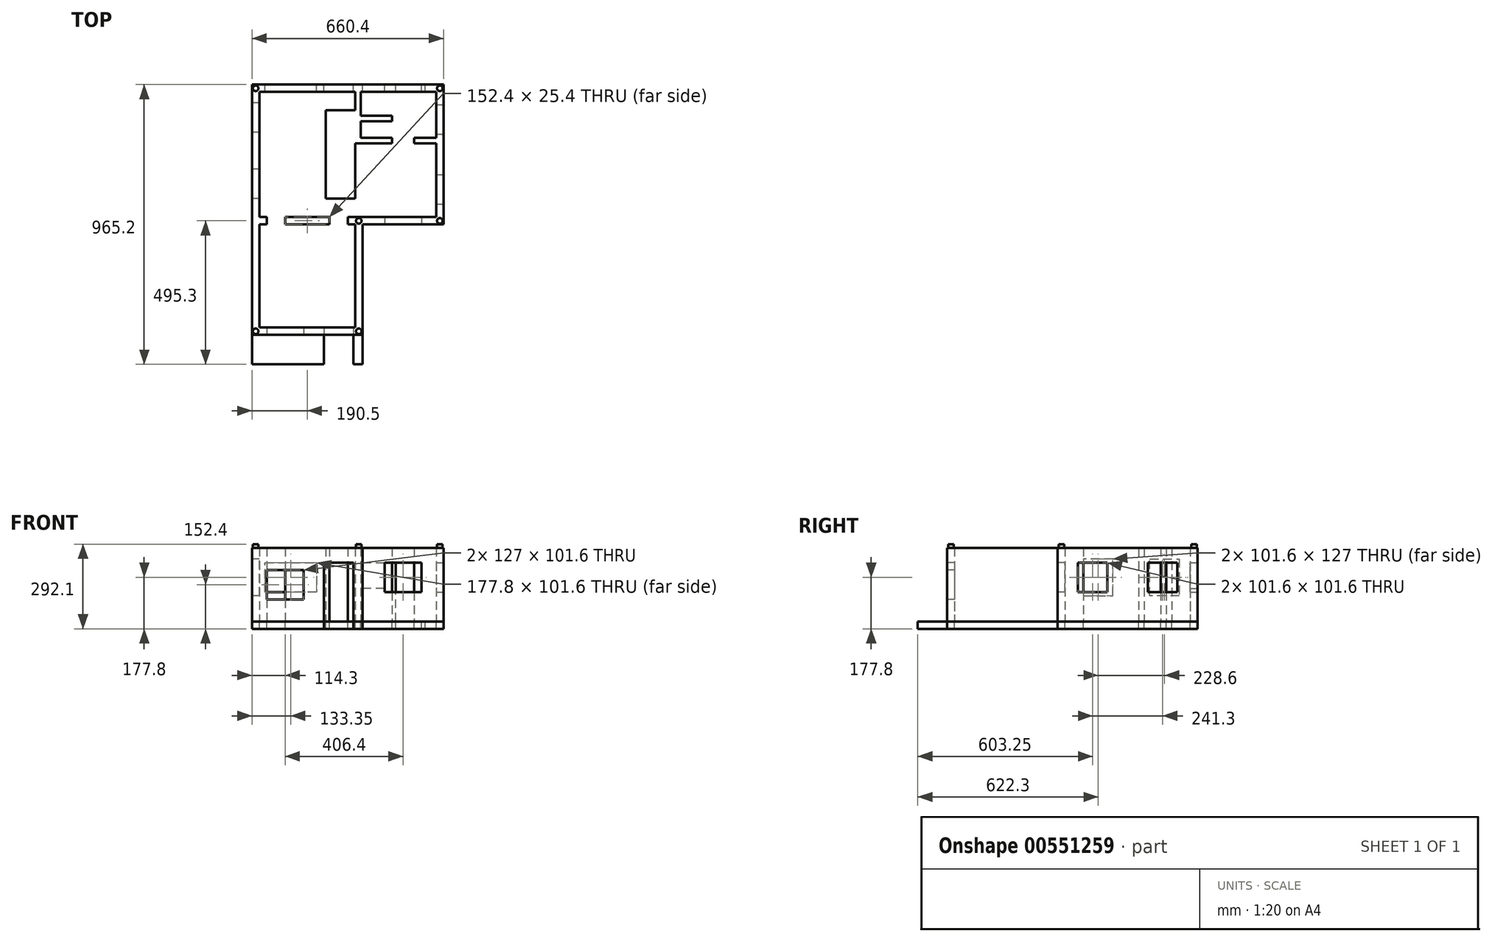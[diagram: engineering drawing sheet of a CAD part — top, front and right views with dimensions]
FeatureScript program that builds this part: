
annotation { "Feature Type Name" : "Feature", "Feature Type Description" : "" }
export const myFeature = defineFeature(function(context is Context, id is Id, definition is map)
    precondition{}
    {
        {
            var Q0;
            Q0=qCreatedBy(makeId("Top.planeOp"),FACE);
            var sketch = newSketch(context, id + "F0", { "sketchPlane" : qUnion([Q0])});
            skLineSegment(sketch, "E0", {"start": v(0, 0) * mm, "end": v(330.2, 0) * mm});
            skLineSegment(sketch, "E1", {"start": v(0, 0) * mm, "end": v(0, 381) * mm});
            skLineSegment(sketch, "E2", {"start": v(330.2, 0) * mm, "end": v(330.2, 381) * mm});
            skLineSegment(sketch, "E3", {"start": v(0, 381) * mm, "end": v(0, 812.8) * mm});
            skLineSegment(sketch, "E4", {"start": v(0, 812.8) * mm, "end": v(330.2, 812.8) * mm});
            skLineSegment(sketch, "E5", {"start": v(330.2, 381) * mm, "end": v(609.6, 381) * mm});
            skLineSegment(sketch, "E6", {"start": v(609.6, 381) * mm, "end": v(609.6, 812.8) * mm});
            skLineSegment(sketch, "E7", {"start": v(609.6, 635) * mm, "end": v(533.4, 635) * mm});
            skLineSegment(sketch, "E8", {"start": v(609.6, 812.8) * mm, "end": v(508, 812.8) * mm});
            skLineSegment(sketch, "E9", {"start": v(330.2, 812.8) * mm, "end": v(508, 812.8) * mm});
            skLineSegment(sketch, "E10", {"start": v(330.2, 672.42) * mm, "end": v(330.2, 812.8) * mm});
            skLineSegment(sketch, "E11", {"start": v(330.2, 635) * mm, "end": v(457.2, 635) * mm});
            skLineSegment(sketch, "E12", {"start": v(457.2, 711.2) * mm, "end": v(330.2, 711.2) * mm});
            skLineSegment(sketch, "E13", {"start": v(330.2, 0) * mm, "end": v(355.6, 0) * mm});
            skLineSegment(sketch, "E14", {"start": v(355.6, 0) * mm, "end": v(355.6, 355.6) * mm});
            skLineSegment(sketch, "E15", {"start": v(355.6, 355.6) * mm, "end": v(635, 355.6) * mm});
            skLineSegment(sketch, "E16", {"start": v(635, 355.6) * mm, "end": v(635, 838.2) * mm});
            skLineSegment(sketch, "E17", {"start": v(635, 838.2) * mm, "end": v(-25.4, 838.2) * mm});
            skLineSegment(sketch, "E18", {"start": v(-25.4, 838.2) * mm, "end": v(-25.4, -25.4) * mm});
            skLineSegment(sketch, "E19", {"start": v(-25.4, -25.4) * mm, "end": v(355.6, -25.4) * mm});
            skLineSegment(sketch, "E20", {"start": v(355.6, -25.4) * mm, "end": v(355.6, 0) * mm});
            skLineSegment(sketch, "E21", {"start": v(0, 381) * mm, "end": v(25.4, 381) * mm});
            skLineSegment(sketch, "E22", {"start": v(25.4, 381) * mm, "end": v(25.4, 355.6) * mm});
            skLineSegment(sketch, "E23", {"start": v(25.4, 355.6) * mm, "end": v(0, 355.6) * mm});
            skLineSegment(sketch, "E24", {"start": v(88.9, 381) * mm, "end": v(241.3, 381) * mm});
            skLineSegment(sketch, "E25", {"start": v(88.9, 381) * mm, "end": v(88.9, 355.6) * mm});
            skLineSegment(sketch, "E26", {"start": v(88.9, 355.6) * mm, "end": v(241.3, 355.6) * mm});
            skLineSegment(sketch, "E27", {"start": v(241.3, 355.6) * mm, "end": v(241.3, 381) * mm});
            skLineSegment(sketch, "E28", {"start": v(304.8, 355.6) * mm, "end": v(304.8, 381) * mm});
            skLineSegment(sketch, "E29", {"start": v(304.8, 381) * mm, "end": v(330.2, 381) * mm});
            skLineSegment(sketch, "E30", {"start": v(304.8, 355.6) * mm, "end": v(330.2, 355.6) * mm});
            skLineSegment(sketch, "E31", {"start": v(330.2, 672.42) * mm, "end": v(330.2, 635) * mm});
            skLineSegment(sketch, "E32", {"start": v(228.6, 749.3) * mm, "end": v(330.2, 749.3) * mm});
            skLineSegment(sketch, "E33", {"start": v(330.2, 635) * mm, "end": v(330.2, 444.5) * mm});
            skLineSegment(sketch, "E34", {"start": v(330.2, 444.5) * mm, "end": v(228.6, 444.5) * mm});
            skLineSegment(sketch, "E35", {"start": v(228.6, 444.5) * mm, "end": v(228.6, 749.3) * mm});
            skLineSegment(sketch, "E36", {"start": v(457.2, 711.2) * mm, "end": v(457.2, 730.25) * mm});
            skLineSegment(sketch, "E37", {"start": v(457.2, 635) * mm, "end": v(457.2, 654.05) * mm});
            skLineSegment(sketch, "E38", {"start": v(457.2, 654.05) * mm, "end": v(349.25, 654.05) * mm});
            skLineSegment(sketch, "E39", {"start": v(349.25, 654.05) * mm, "end": v(349.25, 711.2) * mm});
            skLineSegment(sketch, "E40", {"start": v(533.4, 635) * mm, "end": v(533.4, 654.05) * mm});
            skLineSegment(sketch, "E41", {"start": v(533.4, 654.05) * mm, "end": v(609.6, 654.05) * mm});
            skLineSegment(sketch, "E42", {"start": v(457.2, 730.25) * mm, "end": v(349.25, 730.25) * mm});
            skLineSegment(sketch, "E43", {"start": v(349.25, 730.25) * mm, "end": v(349.25, 812.8) * mm});
            skSolve(sketch);
        }
        {
            var Q0;
            {var subQ8=sQuery(id+"F0.wireOp",EDGE,"E0");Q0=makeQuery(id+"F0.imprint","IMPRINT",FACE,{"disambiguationData":[TD([[makeQuery(id+"F0.imprint","IMPRINT",EDGE,{"derivedFrom":subQ8}),-1.0]])]});}
            var Q1;
            Q1=makeQuery(id+"F0.imprint","IMPRINT",FACE,{"disambiguationData":[TD([[makeQuery(id+"F0.imprint","IMPRINT",EDGE,{"derivedFrom":sQuery(id+"F0.wireOp",EDGE,"E24")}),-1.0]])]});
            var Q2;
            {var subQ0=sQuery(id+"F0.wireOp",EDGE,"E21");Q2=makeQuery(id+"F0.imprint","IMPRINT",FACE,{"disambiguationData":[TD([[makeQuery(id+"F0.imprint","IMPRINT",EDGE,{"derivedFrom":subQ0}),-1.0]])]});}
            var Q3;
            Q3=makeQuery(id+"F0.imprint","IMPRINT",FACE,{"disambiguationData":[TD([[makeQuery(id+"F0.imprint","IMPRINT",EDGE,{"derivedFrom":sQuery(id+"F0.wireOp",EDGE,"E28")}),-1.0]])]});
            var Q4;
            {var subQ3=sQuery(id+"F0.wireOp",EDGE,"E31");Q4=makeQuery(id+"F0.imprint","IMPRINT",FACE,{"disambiguationData":[TD([[makeQuery(id+"F0.imprint","IMPRINT",EDGE,{"derivedFrom":subQ3}),-1.0]])]});}
            var Q5;
            {var subQ0=sQuery(id+"F0.wireOp",EDGE,"E36");Q5=makeQuery(id+"F0.imprint","IMPRINT",FACE,{"disambiguationData":[TD([[makeQuery(id+"F0.imprint","IMPRINT",EDGE,{"derivedFrom":subQ0}),1.0]])]});}
            var Q6;
            Q6=makeQuery(id+"F0.imprint","IMPRINT",FACE,{"disambiguationData":[TD([[makeQuery(id+"F0.imprint","IMPRINT",EDGE,{"derivedFrom":sQuery(id+"F0.wireOp",EDGE,"E11")}),1.0]])]});
            var Q7;
            {var subQ0=sQuery(id+"F0.wireOp",EDGE,"E7");Q7=makeQuery(id+"F0.imprint","IMPRINT",FACE,{"disambiguationData":[TD([[makeQuery(id+"F0.imprint","IMPRINT",EDGE,{"derivedFrom":subQ0}),-1.0]])]});}
            extrude(context, id + "F1", {"entities" : qUnion([Q0, Q1, Q2, Q3, Q4, Q5, Q6, Q7]), "depth" : 254 * mm, "offsetDistance" : 25.4 * mm});
        }
        {
            var Q0;
            {var subQ10=sQuery(id+"F0.wireOp",EDGE,"E0");Q0=makeQuery(id+"F0.imprint","IMPRINT",FACE,{"disambiguationData":[TD([[makeQuery(id+"F0.imprint","IMPRINT",EDGE,{"derivedFrom":subQ10}),1.0]])]});}
            extrude(context, id + "F2", {"entities" : qUnion([Q0]), "oppositeDirection" : true, "depth" : 25.4 * mm, "offsetDistance" : 25.4 * mm});
        }
        {
            var Q0;
            Q0=makeQuery(id+"F1.opExtrude","CAP_FACE",FACE,{"disambiguationData":[OSD([sQuery(id+"F0.wireOp",EDGE,"E0"),sQuery(id+"F0.wireOp",EDGE,"E1"),sQuery(id+"F0.wireOp",EDGE,"E2"),sQuery(id+"F0.wireOp",EDGE,"E3"),sQuery(id+"F0.wireOp",EDGE,"E4"),sQuery(id+"F0.wireOp",EDGE,"E5"),sQuery(id+"F0.wireOp",EDGE,"E6"),sQuery(id+"F0.wireOp",EDGE,"E7"),sQuery(id+"F0.wireOp",EDGE,"E8"),sQuery(id+"F0.wireOp",EDGE,"E9"),sQuery(id+"F0.wireOp",EDGE,"E10"),sQuery(id+"F0.wireOp",EDGE,"E11"),sQuery(id+"F0.wireOp",EDGE,"E12"),sQuery(id+"F0.wireOp",EDGE,"E14"),sQuery(id+"F0.wireOp",EDGE,"E15"),sQuery(id+"F0.wireOp",EDGE,"E16"),sQuery(id+"F0.wireOp",EDGE,"E17"),sQuery(id+"F0.wireOp",EDGE,"E18"),sQuery(id+"F0.wireOp",EDGE,"E19"),sQuery(id+"F0.wireOp",EDGE,"E20"),sQuery(id+"F0.wireOp",EDGE,"E21"),sQuery(id+"F0.wireOp",EDGE,"E22"),sQuery(id+"F0.wireOp",EDGE,"E23"),sQuery(id+"F0.wireOp",EDGE,"E28"),sQuery(id+"F0.wireOp",EDGE,"E29"),sQuery(id+"F0.wireOp",EDGE,"E30"),sQuery(id+"F0.wireOp",EDGE,"E32"),sQuery(id+"F0.wireOp",EDGE,"E33"),sQuery(id+"F0.wireOp",EDGE,"E34"),sQuery(id+"F0.wireOp",EDGE,"E35"),sQuery(id+"F0.wireOp",EDGE,"E36"),sQuery(id+"F0.wireOp",EDGE,"E37"),sQuery(id+"F0.wireOp",EDGE,"E38"),sQuery(id+"F0.wireOp",EDGE,"E39"),sQuery(id+"F0.wireOp",EDGE,"E40"),sQuery(id+"F0.wireOp",EDGE,"E41"),sQuery(id+"F0.wireOp",EDGE,"E42"),sQuery(id+"F0.wireOp",EDGE,"E43")])],"isStart":false});
            var sketch = newSketch(context, id + "F3", { "sketchPlane" : qUnion([Q0])});
            skLineSegment(sketch, "E44", {"start": v(0, 0) * mm, "end": v(-25.4, 0) * mm});
            skLineSegment(sketch, "E45", {"start": v(0, 0) * mm, "end": v(0, -25.4) * mm});
            skLineSegment(sketch, "E46", {"start": v(330.2, 0) * mm, "end": v(330.2, -25.4) * mm});
            skLineSegment(sketch, "E47", {"start": v(330.2, 0) * mm, "end": v(355.6, 0) * mm});
            skLineSegment(sketch, "E48", {"start": v(330.2, 355.6) * mm, "end": v(330.2, 381) * mm});
            skLineSegment(sketch, "E49", {"start": v(330.2, 355.6) * mm, "end": v(355.6, 355.6) * mm});
            skLineSegment(sketch, "E50", {"start": v(355.6, 355.6) * mm, "end": v(355.6, 381) * mm});
            skLineSegment(sketch, "E51", {"start": v(609.6, 381) * mm, "end": v(609.6, 355.6) * mm});
            skLineSegment(sketch, "E52", {"start": v(609.6, 381) * mm, "end": v(635, 381) * mm});
            skLineSegment(sketch, "E53", {"start": v(609.6, 812.8) * mm, "end": v(609.6, 838.2) * mm});
            skLineSegment(sketch, "E54", {"start": v(609.6, 812.8) * mm, "end": v(635, 812.8) * mm});
            skLineSegment(sketch, "E55", {"start": v(-25.4, 812.8) * mm, "end": v(0, 812.8) * mm});
            skLineSegment(sketch, "E56", {"start": v(0, 812.8) * mm, "end": v(0, 838.2) * mm});
            skCircle(sketch, "E57", {"center": v(-12.7, -12.7) * mm, "radius": 9.53 * mm});
            skPoint(sketch, "E57.centerSnap0", {"position": v(-12.7, 0) * mm});
            skPoint(sketch, "E57.centerSnap1", {"position": v(0, -12.7) * mm});
            skPoint(sketch, "E58.centerSnap0", {"position": v(330.2, -12.7) * mm});
            skPoint(sketch, "E58.centerSnap1", {"position": v(342.9, 0) * mm});
            skCircle(sketch, "E59", {"center": v(342.9, -12.7) * mm, "radius": 9.53 * mm});
            skCircle(sketch, "E60", {"center": v(342.9, 368.3) * mm, "radius": 9.53 * mm});
            skPoint(sketch, "E60.centerSnap0", {"position": v(342.9, 355.6) * mm});
            skPoint(sketch, "E60.centerSnap1", {"position": v(330.2, 368.3) * mm});
            skCircle(sketch, "E61", {"center": v(622.3, 368.3) * mm, "radius": 9.53 * mm});
            skPoint(sketch, "E61.centerSnap0", {"position": v(609.6, 368.3) * mm});
            skPoint(sketch, "E61.centerSnap1", {"position": v(622.3, 381) * mm});
            skCircle(sketch, "E62", {"center": v(622.3, 825.5) * mm, "radius": 9.53 * mm});
            skPoint(sketch, "E62.centerSnap0", {"position": v(609.6, 825.5) * mm});
            skPoint(sketch, "E62.centerSnap1", {"position": v(622.3, 812.8) * mm});
            skCircle(sketch, "E63", {"center": v(-12.7, 825.5) * mm, "radius": 9.53 * mm});
            skPoint(sketch, "E63.centerSnap0", {"position": v(-12.7, 812.8) * mm});
            skPoint(sketch, "E63.centerSnap1", {"position": v(0, 825.5) * mm});
            skSolve(sketch);
        }
        {
            var Q0;
            Q0 = qSketchRegion(id + "F3", true);
            extrude(context, id + "F4", {"entities" : qUnion([Q0]), "operationType" : NewBodyOperationType.ADD, "depth" : 12.7 * mm, "offsetDistance" : 25.4 * mm});
        }
        {
            var Q0;
            Q0=makeQuery(id+"F1.opExtrude","SWEPT_FACE",FACE,{"disambiguationData":[OSD([sQuery(id+"F0.wireOp",EDGE,"E19")])]});
            var sketch = newSketch(context, id + "F5", { "sketchPlane" : qUnion([Q0])});
            skLineSegment(sketch, "E64", {"start": v(-25.4, 0) * mm, "end": v(-25.4, 76.2) * mm});
            skLineSegment(sketch, "E65", {"start": v(25.4, 76.2) * mm, "end": v(152.4, 76.2) * mm});
            skLineSegment(sketch, "E66", {"start": v(152.4, 76.2) * mm, "end": v(152.4, 177.8) * mm});
            skLineSegment(sketch, "E67", {"start": v(152.4, 177.8) * mm, "end": v(25.4, 177.8) * mm});
            skLineSegment(sketch, "E68", {"start": v(25.4, 177.8) * mm, "end": v(25.4, 76.2) * mm});
            skSolve(sketch);
        }
        {
            var Q0;
            Q0=makeQuery(id+"F5.imprint","IMPRINT",FACE,{"disambiguationData":[TD([[makeQuery(id+"F5.imprint","IMPRINT",EDGE,{"derivedFrom":sQuery(id+"F5.wireOp",EDGE,"E65")}),1.0]])]});
            extrude(context, id + "F6", {"entities" : qUnion([Q0]), "operationType" : NewBodyOperationType.REMOVE, "oppositeDirection" : true, "depth" : 25.4 * mm, "offsetDistance" : 25.4 * mm});
        }
        {
            var Q0;
            Q0=makeQuery(id+"F1.opExtrude","SWEPT_FACE",FACE,{"disambiguationData":[OSD([sQuery(id+"F0.wireOp",EDGE,"E19")])]});
            var sketch = newSketch(context, id + "F7", { "sketchPlane" : qUnion([Q0])});
            skLineSegment(sketch, "E69", {"start": v(323.85, 0) * mm, "end": v(323.85, 203.2) * mm});
            skLineSegment(sketch, "E70", {"start": v(323.85, 203.2) * mm, "end": v(222.25, 203.2) * mm});
            skLineSegment(sketch, "E71", {"start": v(222.25, 203.2) * mm, "end": v(222.25, 0) * mm});
            skLineSegment(sketch, "E72", {"start": v(222.25, 0) * mm, "end": v(323.85, 0) * mm});
            skSolve(sketch);
        }
        {
            var Q0;
            Q0 = qSketchRegion(id + "F7", true);
            extrude(context, id + "F8", {"entities" : qUnion([Q0]), "operationType" : NewBodyOperationType.REMOVE, "oppositeDirection" : true, "depth" : 25.4 * mm, "offsetDistance" : 25.4 * mm});
        }
        {
            var Q0;
            Q0=makeQuery(id+"F1.opExtrude","SWEPT_FACE",FACE,{"disambiguationData":[OSD([sQuery(id+"F0.wireOp",EDGE,"E15")])]});
            var sketch = newSketch(context, id + "F9", { "sketchPlane" : qUnion([Q0])});
            skLineSegment(sketch, "E73", {"start": v(395.93, 254) * mm, "end": v(395.93, 0) * mm});
            skLineSegment(sketch, "E74", {"start": v(355.6, 231.93) * mm, "end": v(635, 231.93) * mm});
            skPoint(sketch, "E75.startSnap0", {"position": v(395.93, 127) * mm});
            skPoint(sketch, "E75.startSnap1", {"position": v(495.3, 231.93) * mm});
            skLineSegment(sketch, "E76", {"start": v(495.3, 101.6) * mm, "end": v(431.8, 101.6) * mm});
            skLineSegment(sketch, "E77", {"start": v(431.8, 101.6) * mm, "end": v(431.8, 203.2) * mm});
            skLineSegment(sketch, "E78", {"start": v(431.8, 203.2) * mm, "end": v(558.8, 203.2) * mm});
            skLineSegment(sketch, "E79", {"start": v(558.8, 203.2) * mm, "end": v(558.8, 101.6) * mm});
            skLineSegment(sketch, "E80", {"start": v(558.8, 101.6) * mm, "end": v(495.3, 101.6) * mm});
            skSolve(sketch);
        }
        {
            var Q0;
            Q0 = qSketchRegion(id + "F9", true);
            extrude(context, id + "F10", {"entities" : qUnion([Q0]), "operationType" : NewBodyOperationType.REMOVE, "oppositeDirection" : true, "depth" : 25.4 * mm, "offsetDistance" : 25.4 * mm});
        }
        {
            var Q0;
            Q0=makeQuery(id+"F1.opExtrude","SWEPT_FACE",FACE,{"disambiguationData":[OSD([sQuery(id+"F0.wireOp",EDGE,"E16")])]});
            var sketch = newSketch(context, id + "F11", { "sketchPlane" : qUnion([Q0])});
            skLineSegment(sketch, "E81", {"start": v(355.6, 254) * mm, "end": v(838.2, 254) * mm});
            skLineSegment(sketch, "E82", {"start": v(596.9, 254) * mm, "end": v(596.9, 0) * mm});
            skLineSegment(sketch, "E83", {"start": v(355.6, 254) * mm, "end": v(596.9, 254) * mm});
            skLineSegment(sketch, "E84", {"start": v(476.25, 203.2) * mm, "end": v(425.45, 203.2) * mm});
            skLineSegment(sketch, "E85", {"start": v(425.45, 203.2) * mm, "end": v(425.45, 101.6) * mm});
            skLineSegment(sketch, "E86", {"start": v(425.45, 101.6) * mm, "end": v(527.05, 101.6) * mm});
            skLineSegment(sketch, "E87", {"start": v(527.05, 101.6) * mm, "end": v(527.05, 203.2) * mm});
            skLineSegment(sketch, "E88", {"start": v(527.05, 203.2) * mm, "end": v(476.25, 203.2) * mm});
            skLineSegment(sketch, "E89", {"start": v(596.9, 254) * mm, "end": v(838.2, 254) * mm});
            skLineSegment(sketch, "E90", {"start": v(717.55, 203.2) * mm, "end": v(666.75, 203.2) * mm});
            skLineSegment(sketch, "E91", {"start": v(666.75, 203.2) * mm, "end": v(666.75, 101.6) * mm});
            skLineSegment(sketch, "E92", {"start": v(666.75, 101.6) * mm, "end": v(768.35, 101.6) * mm});
            skLineSegment(sketch, "E93", {"start": v(768.35, 101.6) * mm, "end": v(768.35, 203.2) * mm});
            skLineSegment(sketch, "E94", {"start": v(768.35, 203.2) * mm, "end": v(717.55, 203.2) * mm});
            skSolve(sketch);
        }
        {
            var Q0;
            Q0 = qSketchRegion(id + "F11", true);
            extrude(context, id + "F12", {"entities" : qUnion([Q0]), "operationType" : NewBodyOperationType.REMOVE, "oppositeDirection" : true, "depth" : 25.4 * mm, "offsetDistance" : 25.4 * mm});
        }
        {
            var Q0;
            Q0 = qSketchRegion(id + "F11", true);
            extrude(context, id + "F13", {"entities" : qUnion([Q0]), "operationType" : NewBodyOperationType.REMOVE, "oppositeDirection" : true, "depth" : 25.4 * mm, "offsetDistance" : 25.4 * mm});
        }
        {
            var Q0;
            Q0=makeQuery(id+"F1.opExtrude","SWEPT_FACE",FACE,{"disambiguationData":[OSD([sQuery(id+"F0.wireOp",EDGE,"E18")])]});
            var sketch = newSketch(context, id + "F14", { "sketchPlane" : qUnion([Q0])});
            skLineSegment(sketch, "E95", {"start": v(-838.2, 254) * mm, "end": v(-381, 254) * mm});
            skLineSegment(sketch, "E96", {"start": v(-381, 254) * mm, "end": v(-381, 0) * mm});
            skLineSegment(sketch, "E97", {"start": v(-609.6, 254) * mm, "end": v(-609.6, 0) * mm});
            skLineSegment(sketch, "E98", {"start": v(-838.2, 254) * mm, "end": v(-609.6, 254) * mm});
            skLineSegment(sketch, "E99", {"start": v(-723.9, 215.9) * mm, "end": v(-774.7, 215.9) * mm});
            skLineSegment(sketch, "E100", {"start": v(-774.7, 215.9) * mm, "end": v(-774.7, 88.9) * mm});
            skLineSegment(sketch, "E101", {"start": v(-774.7, 88.9) * mm, "end": v(-673.1, 88.9) * mm});
            skLineSegment(sketch, "E102", {"start": v(-673.1, 88.9) * mm, "end": v(-673.1, 215.9) * mm});
            skLineSegment(sketch, "E103", {"start": v(-673.1, 215.9) * mm, "end": v(-723.9, 215.9) * mm});
            skLineSegment(sketch, "E104.MirrorCS", {"start": v(-546.1, 88.9) * mm, "end": v(-546.1, 215.9) * mm});
            skLineSegment(sketch, "E105.MirrorCS", {"start": v(-546.1, 215.9) * mm, "end": v(-495.3, 215.9) * mm});
            skLineSegment(sketch, "E106.MirrorCS", {"start": v(-495.3, 215.9) * mm, "end": v(-444.5, 215.9) * mm});
            skLineSegment(sketch, "E107.MirrorCS", {"start": v(-444.5, 215.9) * mm, "end": v(-444.5, 88.9) * mm});
            skLineSegment(sketch, "E108.MirrorCS", {"start": v(-444.5, 88.9) * mm, "end": v(-546.1, 88.9) * mm});
            skSolve(sketch);
        }
        {
            var Q0;
            Q0 = qSketchRegion(id + "F14", true);
            extrude(context, id + "F15", {"entities" : qUnion([Q0]), "operationType" : NewBodyOperationType.REMOVE, "oppositeDirection" : true, "depth" : 25.4 * mm, "offsetDistance" : 25.4 * mm});
        }
        {
            var Q0;
            Q0 = qSketchRegion(id + "F14", true);
            extrude(context, id + "F16", {"entities" : qUnion([Q0]), "operationType" : NewBodyOperationType.REMOVE, "oppositeDirection" : true, "depth" : 25.4 * mm, "offsetDistance" : 25.4 * mm});
        }
        {
            var Q0;
            Q0=makeQuery(id+"F1.opExtrude","SWEPT_FACE",FACE,{"disambiguationData":[OSD([sQuery(id+"F0.wireOp",EDGE,"E17")])]});
            var sketch = newSketch(context, id + "F17", { "sketchPlane" : qUnion([Q0])});
            skLineSegment(sketch, "E109", {"start": v(25.4, 254) * mm, "end": v(-330.2, 254) * mm});
            skLineSegment(sketch, "E110", {"start": v(-330.2, 254) * mm, "end": v(-330.2, 0) * mm});
            skPoint(sketch, "E111.endSnap0", {"position": v(-152.4, 254) * mm});
            skLineSegment(sketch, "E112", {"start": v(-222.25, 0) * mm, "end": v(-222.25, 203.2) * mm});
            skLineSegment(sketch, "E113", {"start": v(-222.25, 203.2) * mm, "end": v(-323.85, 203.2) * mm});
            skLineSegment(sketch, "E114", {"start": v(-323.85, 203.2) * mm, "end": v(-323.85, 0) * mm});
            skLineSegment(sketch, "E115", {"start": v(-323.85, 0) * mm, "end": v(-222.25, 0) * mm});
            skLineSegment(sketch, "E116", {"start": v(-196.85, 203.2) * mm, "end": v(-196.85, 101.6) * mm});
            skLineSegment(sketch, "E117", {"start": v(-196.85, 101.6) * mm, "end": v(-19.05, 101.6) * mm});
            skLineSegment(sketch, "E118", {"start": v(-19.05, 101.6) * mm, "end": v(-19.05, 203.2) * mm});
            skLineSegment(sketch, "E119", {"start": v(-19.05, 203.2) * mm, "end": v(-196.85, 203.2) * mm});
            skSolve(sketch);
        }
        {
            var Q0;
            Q0 = qSketchRegion(id + "F17", true);
            extrude(context, id + "F18", {"entities" : qUnion([Q0]), "operationType" : NewBodyOperationType.REMOVE, "oppositeDirection" : true, "depth" : 25.4 * mm, "offsetDistance" : 25.4 * mm});
        }
        {
            var Q0;
            Q0 = qSketchRegion(id + "F17", true);
            extrude(context, id + "F19", {"entities" : qUnion([Q0]), "operationType" : NewBodyOperationType.REMOVE, "oppositeDirection" : true, "depth" : 25.4 * mm, "offsetDistance" : 25.4 * mm});
        }
        {
            var Q0;
            Q0=makeQuery(id+"F1.opExtrude","SWEPT_FACE",FACE,{"disambiguationData":[OSD([sQuery(id+"F0.wireOp",EDGE,"E17")])]});
            var sketch = newSketch(context, id + "F20", { "sketchPlane" : qUnion([Q0])});
            skLineSegment(sketch, "E120", {"start": v(-635, 254) * mm, "end": v(-355.6, 254) * mm});
            skLineSegment(sketch, "E121", {"start": v(-355.6, 139.7) * mm, "end": v(-355.6, 203.2) * mm});
            skLineSegment(sketch, "E122", {"start": v(-355.6, 203.2) * mm, "end": v(-431.8, 203.2) * mm});
            skLineSegment(sketch, "E123", {"start": v(-431.8, 203.2) * mm, "end": v(-431.8, 114.3) * mm});
            skLineSegment(sketch, "E124", {"start": v(-431.8, 114.3) * mm, "end": v(-355.6, 114.3) * mm});
            skLineSegment(sketch, "E125", {"start": v(-355.6, 114.3) * mm, "end": v(-355.6, 139.7) * mm});
            skLineSegment(sketch, "E126", {"start": v(-431.8, 114.3) * mm, "end": v(-469.9, 114.3) * mm});
            skLineSegment(sketch, "E127", {"start": v(-469.9, 114.3) * mm, "end": v(-469.9, 203.2) * mm});
            skLineSegment(sketch, "E128", {"start": v(-469.9, 203.2) * mm, "end": v(-558.8, 203.2) * mm});
            skLineSegment(sketch, "E129", {"start": v(-558.8, 203.2) * mm, "end": v(-558.8, 0) * mm});
            skLineSegment(sketch, "E130", {"start": v(-558.8, 0) * mm, "end": v(-469.9, 0) * mm});
            skLineSegment(sketch, "E131", {"start": v(-469.9, 0) * mm, "end": v(-469.9, 114.3) * mm});
            skSolve(sketch);
        }
        {
            var Q0;
            Q0=makeQuery(id+"F20.imprint","IMPRINT",FACE,{"disambiguationData":[TD([[makeQuery(id+"F20.imprint","IMPRINT",EDGE,{"derivedFrom":sQuery(id+"F20.wireOp",EDGE,"E121")}),1.0]])]});
            extrude(context, id + "F21", {"entities" : qUnion([Q0]), "operationType" : NewBodyOperationType.REMOVE, "oppositeDirection" : true, "depth" : 25.4 * mm, "offsetDistance" : 25.4 * mm});
        }
        {
            var Q0;
            Q0 = qSketchRegion(id + "F20", true);
            extrude(context, id + "F22", {"entities" : qUnion([Q0]), "operationType" : NewBodyOperationType.REMOVE, "oppositeDirection" : true, "depth" : 25.4 * mm, "offsetDistance" : 25.4 * mm});
        }
        {
            var Q0;
            {var subQ0=sQuery(id+"F0.wireOp",EDGE,"E32");var subQ2=sQuery(id+"F0.wireOp",EDGE,"E17");var subQ4=sQuery(id+"F0.wireOp",EDGE,"E12");var subQ6=sQuery(id+"F0.wireOp",EDGE,"E37");var subQ8=sQuery(id+"F0.wireOp",EDGE,"E4");var subQ9=makeQuery(id+"F1.opExtrude","SWEPT_FACE",FACE,{"disambiguationData":[OSD([subQ8])]});var subQ10=sQuery(id+"F0.wireOp",EDGE,"E33");var subQ12=sQuery(id+"F0.wireOp",EDGE,"E9");var subQ13=sQuery(id+"F0.wireOp",EDGE,"E8");var subQ15=sQuery(id+"F0.wireOp",EDGE,"E34");var subQ17=sQuery(id+"F0.wireOp",EDGE,"E10");var subQ19=sQuery(id+"F0.wireOp",EDGE,"E35");var subQ21=sQuery(id+"F0.wireOp",EDGE,"E11");var subQ23=sQuery(id+"F0.wireOp",EDGE,"E36");var subQ26=sQuery(id+"F0.wireOp",EDGE,"E38");var subQ28=sQuery(id+"F0.wireOp",EDGE,"E39");var subQ30=sQuery(id+"F0.wireOp",EDGE,"E42");var subQ32=sQuery(id+"F0.wireOp",EDGE,"E43");var subQ34=sQuery(id+"F0.wireOp",EDGE,"E19");var subQ35=sQuery(id+"F0.wireOp",EDGE,"E16");var subQ36=sQuery(id+"F0.wireOp",EDGE,"E15");var subQ37=sQuery(id+"F0.wireOp",EDGE,"E20");var subQ38=sQuery(id+"F0.wireOp",EDGE,"E14");var subQ39=sQuery(id+"F0.wireOp",EDGE,"E28");var subQ40=sQuery(id+"F0.wireOp",EDGE,"E29");var subQ41=sQuery(id+"F0.wireOp",EDGE,"E5");var subQ42=sQuery(id+"F0.wireOp",EDGE,"E2");var subQ43=sQuery(id+"F0.wireOp",EDGE,"E0");var subQ44=sQuery(id+"F0.wireOp",EDGE,"E30");var subQ45=sQuery(id+"F0.wireOp",EDGE,"E6");var subQ46=sQuery(id+"F0.wireOp",EDGE,"E7");var subQ47=sQuery(id+"F0.wireOp",EDGE,"E41");var subQ48=sQuery(id+"F0.wireOp",EDGE,"E40");Q0=makeQuery(id+"F22.boolean.opBoolean","SPLIT",FACE,{"disambiguationData":[TD([subQ9])],"derivedFrom":makeQuery(id+"F18.boolean.opBoolean","SPLIT",FACE,{"disambiguationData":[TD([makeQuery(id+"F1.opExtrude","SWEPT_FACE",FACE,{"disambiguationData":[OSD([subQ42])]})])],"derivedFrom":makeQuery(id+"F1.opExtrude","CAP_FACE",FACE,{"disambiguationData":[OSD([subQ43,sQuery(id+"F0.wireOp",EDGE,"E1"),subQ42,sQuery(id+"F0.wireOp",EDGE,"E3"),subQ8,subQ41,subQ45,subQ46,subQ13,subQ12,subQ17,subQ21,subQ4,subQ38,subQ36,subQ35,subQ2,sQuery(id+"F0.wireOp",EDGE,"E18"),subQ34,subQ37,sQuery(id+"F0.wireOp",EDGE,"E21"),sQuery(id+"F0.wireOp",EDGE,"E22"),sQuery(id+"F0.wireOp",EDGE,"E23"),subQ39,subQ40,subQ44,subQ0,subQ10,subQ15,subQ19,subQ23,subQ6,subQ26,subQ28,subQ48,subQ47,subQ30,subQ32])],"isStart":true})})});}
            var Q1;
            {var subQ0=sQuery(id+"F0.wireOp",EDGE,"E16");var subQ2=sQuery(id+"F0.wireOp",EDGE,"E40");var subQ4=sQuery(id+"F0.wireOp",EDGE,"E15");var subQ6=sQuery(id+"F0.wireOp",EDGE,"E7");var subQ8=sQuery(id+"F0.wireOp",EDGE,"E8");var subQ9=sQuery(id+"F0.wireOp",EDGE,"E6");var subQ10=sQuery(id+"F0.wireOp",EDGE,"E41");var subQ12=sQuery(id+"F0.wireOp",EDGE,"E9");var subQ14=sQuery(id+"F0.wireOp",EDGE,"E0");var subQ15=makeQuery(id+"F1.opExtrude","SWEPT_FACE",FACE,{"disambiguationData":[OSD([subQ14])]});var subQ16=sQuery(id+"F0.wireOp",EDGE,"E20");var subQ17=sQuery(id+"F0.wireOp",EDGE,"E14");var subQ19=sQuery(id+"F0.wireOp",EDGE,"E2");var subQ20=makeQuery(id+"F1.opExtrude","SWEPT_FACE",FACE,{"disambiguationData":[OSD([subQ19])]});var subQ21=sQuery(id+"F0.wireOp",EDGE,"E29");var subQ22=sQuery(id+"F0.wireOp",EDGE,"E5");var subQ24=sQuery(id+"F0.wireOp",EDGE,"E28");var subQ27=sQuery(id+"F0.wireOp",EDGE,"E30");var subQ29=sQuery(id+"F0.wireOp",EDGE,"E17");var subQ32=sQuery(id+"F0.wireOp",EDGE,"E19");var subQ35=sQuery(id+"F0.wireOp",EDGE,"E12");var subQ36=sQuery(id+"F0.wireOp",EDGE,"E4");var subQ37=sQuery(id+"F0.wireOp",EDGE,"E34");var subQ38=sQuery(id+"F0.wireOp",EDGE,"E32");var subQ39=sQuery(id+"F0.wireOp",EDGE,"E33");var subQ40=sQuery(id+"F0.wireOp",EDGE,"E35");var subQ41=sQuery(id+"F0.wireOp",EDGE,"E10");var subQ42=sQuery(id+"F0.wireOp",EDGE,"E11");var subQ43=sQuery(id+"F0.wireOp",EDGE,"E36");var subQ44=sQuery(id+"F0.wireOp",EDGE,"E37");var subQ45=sQuery(id+"F0.wireOp",EDGE,"E38");var subQ46=sQuery(id+"F0.wireOp",EDGE,"E39");var subQ47=sQuery(id+"F0.wireOp",EDGE,"E42");var subQ48=sQuery(id+"F0.wireOp",EDGE,"E43");Q1=makeQuery(id+"F22.boolean.opBoolean","SPLIT",FACE,{"disambiguationData":[TD([subQ15])],"derivedFrom":makeQuery(id+"F18.boolean.opBoolean","SPLIT",FACE,{"disambiguationData":[TD([subQ20])],"derivedFrom":makeQuery(id+"F1.opExtrude","CAP_FACE",FACE,{"disambiguationData":[OSD([subQ14,sQuery(id+"F0.wireOp",EDGE,"E1"),subQ19,sQuery(id+"F0.wireOp",EDGE,"E3"),subQ36,subQ22,subQ9,subQ6,subQ8,subQ12,subQ41,subQ42,subQ35,subQ17,subQ4,subQ0,subQ29,sQuery(id+"F0.wireOp",EDGE,"E18"),subQ32,subQ16,sQuery(id+"F0.wireOp",EDGE,"E21"),sQuery(id+"F0.wireOp",EDGE,"E22"),sQuery(id+"F0.wireOp",EDGE,"E23"),subQ24,subQ21,subQ27,subQ38,subQ39,subQ37,subQ40,subQ43,subQ44,subQ45,subQ46,subQ2,subQ10,subQ47,subQ48])],"isStart":true})})});}
            var Q2;
            {var subQ0=sQuery(id+"F0.wireOp",EDGE,"E23");var subQ1=sQuery(id+"F0.wireOp",EDGE,"E0");var subQ2=sQuery(id+"F0.wireOp",EDGE,"E21");var subQ3=sQuery(id+"F0.wireOp",EDGE,"E19");var subQ4=sQuery(id+"F0.wireOp",EDGE,"E18");var subQ5=sQuery(id+"F0.wireOp",EDGE,"E17");var subQ6=sQuery(id+"F0.wireOp",EDGE,"E22");var subQ7=sQuery(id+"F0.wireOp",EDGE,"E3");var subQ8=sQuery(id+"F0.wireOp",EDGE,"E1");var subQ9=sQuery(id+"F0.wireOp",EDGE,"E4");Q2=makeQuery(id+"F18.boolean.opBoolean","SPLIT",FACE,{"disambiguationData":[TD([makeQuery(id+"F1.opExtrude","SWEPT_FACE",FACE,{"disambiguationData":[OSD([subQ8])]})])],"derivedFrom":makeQuery(id+"F1.opExtrude","CAP_FACE",FACE,{"disambiguationData":[OSD([subQ1,subQ8,sQuery(id+"F0.wireOp",EDGE,"E2"),subQ7,subQ9,sQuery(id+"F0.wireOp",EDGE,"E5"),sQuery(id+"F0.wireOp",EDGE,"E6"),sQuery(id+"F0.wireOp",EDGE,"E7"),sQuery(id+"F0.wireOp",EDGE,"E8"),sQuery(id+"F0.wireOp",EDGE,"E9"),sQuery(id+"F0.wireOp",EDGE,"E10"),sQuery(id+"F0.wireOp",EDGE,"E11"),sQuery(id+"F0.wireOp",EDGE,"E12"),sQuery(id+"F0.wireOp",EDGE,"E14"),sQuery(id+"F0.wireOp",EDGE,"E15"),sQuery(id+"F0.wireOp",EDGE,"E16"),subQ5,subQ4,subQ3,sQuery(id+"F0.wireOp",EDGE,"E20"),subQ2,subQ6,subQ0,sQuery(id+"F0.wireOp",EDGE,"E28"),sQuery(id+"F0.wireOp",EDGE,"E29"),sQuery(id+"F0.wireOp",EDGE,"E30"),sQuery(id+"F0.wireOp",EDGE,"E32"),sQuery(id+"F0.wireOp",EDGE,"E33"),sQuery(id+"F0.wireOp",EDGE,"E34"),sQuery(id+"F0.wireOp",EDGE,"E35"),sQuery(id+"F0.wireOp",EDGE,"E36"),sQuery(id+"F0.wireOp",EDGE,"E37"),sQuery(id+"F0.wireOp",EDGE,"E38"),sQuery(id+"F0.wireOp",EDGE,"E39"),sQuery(id+"F0.wireOp",EDGE,"E40"),sQuery(id+"F0.wireOp",EDGE,"E41"),sQuery(id+"F0.wireOp",EDGE,"E42"),sQuery(id+"F0.wireOp",EDGE,"E43")])],"isStart":true})});}
            extrude(context, id + "F23", {"entities" : qUnion([Q0, Q1, Q2]), "depth" : 25.4 * mm, "offsetDistance" : 25.4 * mm});
        }
        {
            var Q0;
            Q0=makeQuery(id+"F23.opExtrude","SWEPT_FACE",FACE,{"disambiguationData":[OSD([sQuery(id+"F0.wireOp",EDGE,"E19"),sQuery(id+"F7.wireOp",EDGE,"E71"),sQuery(id+"F7.wireOp",EDGE,"E72")])]});
            extrude(context, id + "F24", {"entities" : qUnion([Q0]), "depth" : 101.6 * mm, "offsetDistance" : 25.4 * mm});
        }
        {
            var Q0;
            Q0=makeQuery(id+"F23.opExtrude","SWEPT_FACE",FACE,{"disambiguationData":[OSD([sQuery(id+"F0.wireOp",EDGE,"E17"),sQuery(id+"F17.wireOp",EDGE,"E112"),sQuery(id+"F17.wireOp",EDGE,"E115")])]});
            var Q1;
            Q1=makeQuery(id+"F23.opExtrude","SWEPT_FACE",FACE,{"disambiguationData":[OSD([sQuery(id+"F0.wireOp",EDGE,"E17"),sQuery(id+"F20.wireOp",EDGE,"E130"),sQuery(id+"F20.wireOp",EDGE,"E131")])]});
            extrude(context, id + "F25", {"entities" : qUnion([Q0, Q1]), "depth" : 101.6 * mm, "offsetDistance" : 25.4 * mm});
        }
    });
